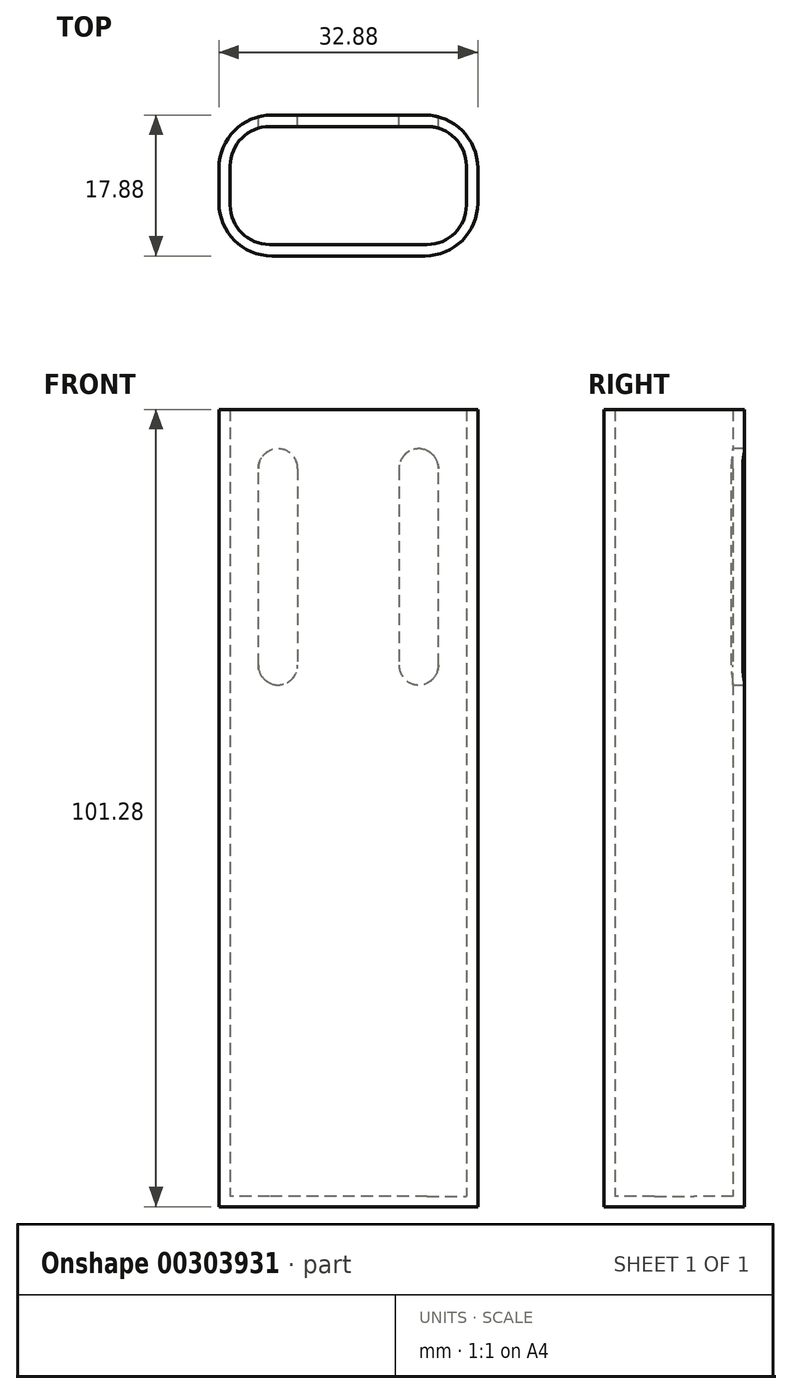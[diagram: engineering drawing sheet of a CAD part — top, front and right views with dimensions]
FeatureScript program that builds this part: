
annotation { "Feature Type Name" : "Feature", "Feature Type Description" : "" }
export const myFeature = defineFeature(function(context is Context, id is Id, definition is map)
    precondition{}
    {
        {
            var Q0;
            Q0=qCreatedBy(makeId("Top.planeOp"),FACE);
            var sketch = newSketch(context, id + "F0", { "sketchPlane" : qUnion([Q0])});
            skLineSegment(sketch, "E0.bottom", {"start": v(0, 0) * mm, "end": v(32.88, 0) * mm});
            skLineSegment(sketch, "E0.top", {"start": v(0, 17.88) * mm, "end": v(32.88, 17.88) * mm});
            skLineSegment(sketch, "E0.left", {"start": v(0, 0) * mm, "end": v(0, 17.88) * mm});
            skLineSegment(sketch, "E0.right", {"start": v(32.88, 0) * mm, "end": v(32.88, 17.88) * mm});
            skSolve(sketch);
        }
        {
            var Q0;
            Q0 = qSketchRegion(id + "F0", true);
            extrude(context, id + "F1", {"entities" : qUnion([Q0]), "depth" : (.32 * 4) * mm});
        }
        {
            var Q0;
            Q0=makeQuery(id+"F1.opExtrude","CAP_FACE",FACE,{"disambiguationData":[OSD([sQuery(id+"F0.wireOp",EDGE,"E0.bottom"),sQuery(id+"F0.wireOp",EDGE,"E0.top"),sQuery(id+"F0.wireOp",EDGE,"E0.left"),sQuery(id+"F0.wireOp",EDGE,"E0.right")])],"isStart":false});
            var sketch = newSketch(context, id + "F2", { "sketchPlane" : qUnion([Q0])});
            skLineSegment(sketch, "E1.0.0", {"start": v(32.88, 17.88) * mm, "end": v(0, 17.88) * mm});
            skLineSegment(sketch, "E1.0.1", {"start": v(0, 17.88) * mm, "end": v(0, 0) * mm});
            skLineSegment(sketch, "E1.0.2", {"start": v(0, 0) * mm, "end": v(32.88, 0) * mm});
            skLineSegment(sketch, "E1.0.3", {"start": v(32.88, 0) * mm, "end": v(32.88, 17.88) * mm});
            skLineSegment(sketch, "E2.0", {"start": v(31.44, 16.44) * mm, "end": v(1.44, 16.44) * mm});
            skLineSegment(sketch, "E2.1", {"start": v(31.44, 1.44) * mm, "end": v(31.44, 16.44) * mm});
            skLineSegment(sketch, "E2.2", {"start": v(1.44, 1.44) * mm, "end": v(31.44, 1.44) * mm});
            skLineSegment(sketch, "E2.3", {"start": v(1.44, 16.44) * mm, "end": v(1.44, 1.44) * mm});
            skSolve(sketch);
        }
        {
            var Q0;
            Q0 = qSketchRegion(id + "F2", true);
            extrude(context, id + "F3", {"entities" : qUnion([Q0]), "operationType" : NewBodyOperationType.ADD, "depth" : 100 * mm});
        }
        {
            var Q0;
            Q0=makeQuery(id+"F3.boolean.opBoolean","MERGE",FACE,{"derivedFrom":[makeQuery(id+"F1.opExtrude","SWEPT_FACE",FACE,{"disambiguationData":[OSD([sQuery(id+"F0.wireOp",EDGE,"E0.top")])]}),makeQuery(id+"F3.opExtrude","SWEPT_FACE",FACE,{"disambiguationData":[OSD([sQuery(id+"F2.wireOp",EDGE,"E1.0.0")])]})]});
            var sketch = newSketch(context, id + "F4", { "sketchPlane" : qUnion([Q0])});
            skLineSegment(sketch, "E3.bottom", {"start": v(-27.88, 96.28) * mm, "end": v(-22.88, 96.28) * mm});
            skLineSegment(sketch, "E3.top", {"start": v(-27.88, 66.28) * mm, "end": v(-22.88, 66.28) * mm});
            skLineSegment(sketch, "E3.left", {"start": v(-27.88, 96.28) * mm, "end": v(-27.88, 66.28) * mm});
            skLineSegment(sketch, "E3.right", {"start": v(-22.88, 96.28) * mm, "end": v(-22.88, 66.28) * mm});
            skLineSegment(sketch, "E4", {"start": v(-16.44, 0) * mm, "end": v(-16.44, 101.28) * mm, "construction": true});
            skLineSegment(sketch, "E5.MirrorCS", {"start": v(-10, 96.28) * mm, "end": v(-10, 66.28) * mm});
            skLineSegment(sketch, "E6.MirrorCS", {"start": v(-5, 96.28) * mm, "end": v(-5, 66.28) * mm});
            skLineSegment(sketch, "E7.MirrorCS", {"start": v(-5, 96.28) * mm, "end": v(-10, 96.28) * mm});
            skLineSegment(sketch, "E8.MirrorCS", {"start": v(-5, 66.28) * mm, "end": v(-10, 66.28) * mm});
            skSolve(sketch);
        }
        {
            var Q0;
            Q0 = qSketchRegion(id + "F4", true);
            extrude(context, id + "F5", {"entities" : qUnion([Q0]), "operationType" : NewBodyOperationType.REMOVE, "endBound" : BoundingType.UP_TO_NEXT, "oppositeDirection" : true, "depth" : 25 * mm});
        }
        {
            var Q0;
            Q0=makeQuery(id+"F3.opExtrude","SWEPT_EDGE",EDGE,{"disambiguationData":[OSD([sQuery(id+"F2.wireOp",EDGE,"E2.2"),sQuery(id+"F2.wireOp",EDGE,"E2.3")])]});
            var Q1;
            Q1=makeQuery(id+"F3.opExtrude","SWEPT_EDGE",EDGE,{"disambiguationData":[OSD([sQuery(id+"F2.wireOp",EDGE,"E2.1"),sQuery(id+"F2.wireOp",EDGE,"E2.2")])]});
            var Q2;
            Q2=makeQuery(id+"F3.opExtrude","SWEPT_EDGE",EDGE,{"disambiguationData":[OSD([sQuery(id+"F2.wireOp",EDGE,"E2.0"),sQuery(id+"F2.wireOp",EDGE,"E2.1")])]});
            var Q3;
            Q3=makeQuery(id+"F3.opExtrude","SWEPT_EDGE",EDGE,{"disambiguationData":[OSD([sQuery(id+"F2.wireOp",EDGE,"E2.0"),sQuery(id+"F2.wireOp",EDGE,"E2.3")])]});
            fillet(context, id + "F6", {"entities" : qUnion([Q0, Q1, Q2, Q3]), "radius" : 5 * mm, "tangentPropagation" : true, "allowEdgeOverflow" : false});
        }
        {
            var Q0;
            Q0=makeQuery(id+"F3.boolean.opBoolean","MERGE",EDGE,{"derivedFrom":[makeQuery(id+"F1.opExtrude","SWEPT_EDGE",EDGE,{"disambiguationData":[OSD([sQuery(id+"F0.wireOp",EDGE,"E0.bottom"),sQuery(id+"F0.wireOp",EDGE,"E0.right")])]}),makeQuery(id+"F3.opExtrude","SWEPT_EDGE",EDGE,{"disambiguationData":[OSD([sQuery(id+"F2.wireOp",EDGE,"E1.0.2"),sQuery(id+"F2.wireOp",EDGE,"E1.0.3")])]})]});
            var Q1;
            Q1=makeQuery(id+"F3.boolean.opBoolean","MERGE",EDGE,{"derivedFrom":[makeQuery(id+"F1.opExtrude","SWEPT_EDGE",EDGE,{"disambiguationData":[OSD([sQuery(id+"F0.wireOp",EDGE,"E0.top"),sQuery(id+"F0.wireOp",EDGE,"E0.right")])]}),makeQuery(id+"F3.opExtrude","SWEPT_EDGE",EDGE,{"disambiguationData":[OSD([sQuery(id+"F2.wireOp",EDGE,"E1.0.0"),sQuery(id+"F2.wireOp",EDGE,"E1.0.3")])]})]});
            var Q2;
            Q2=makeQuery(id+"F3.boolean.opBoolean","MERGE",EDGE,{"derivedFrom":[makeQuery(id+"F1.opExtrude","SWEPT_EDGE",EDGE,{"disambiguationData":[OSD([sQuery(id+"F0.wireOp",EDGE,"E0.bottom"),sQuery(id+"F0.wireOp",EDGE,"E0.left")])]}),makeQuery(id+"F3.opExtrude","SWEPT_EDGE",EDGE,{"disambiguationData":[OSD([sQuery(id+"F2.wireOp",EDGE,"E1.0.1"),sQuery(id+"F2.wireOp",EDGE,"E1.0.2")])]})]});
            var Q3;
            Q3=makeQuery(id+"F3.boolean.opBoolean","MERGE",EDGE,{"derivedFrom":[makeQuery(id+"F1.opExtrude","SWEPT_EDGE",EDGE,{"disambiguationData":[OSD([sQuery(id+"F0.wireOp",EDGE,"E0.top"),sQuery(id+"F0.wireOp",EDGE,"E0.left")])]}),makeQuery(id+"F3.opExtrude","SWEPT_EDGE",EDGE,{"disambiguationData":[OSD([sQuery(id+"F2.wireOp",EDGE,"E1.0.0"),sQuery(id+"F2.wireOp",EDGE,"E1.0.1")])]})]});
            fillet(context, id + "F7", {"entities" : qUnion([Q0, Q1, Q2, Q3]), "radius" : 6.72 * mm, "tangentPropagation" : true, "allowEdgeOverflow" : false});
        }
        {
            var Q0;
            Q0=makeQuery(id+"F5.boolean.opBoolean","COPY",EDGE,{"derivedFrom":makeQuery(id+"F5.opExtrude","SWEPT_EDGE",EDGE,{"disambiguationData":[OSD([sQuery(id+"F4.wireOp",EDGE,"E3.bottom"),sQuery(id+"F4.wireOp",EDGE,"E3.left")])]})});
            var Q1;
            Q1=makeQuery(id+"F5.boolean.opBoolean","COPY",EDGE,{"derivedFrom":makeQuery(id+"F5.opExtrude","SWEPT_EDGE",EDGE,{"disambiguationData":[OSD([sQuery(id+"F4.wireOp",EDGE,"E5.MirrorCS"),sQuery(id+"F4.wireOp",EDGE,"E7.MirrorCS")])]})});
            var Q2;
            Q2=makeQuery(id+"F5.boolean.opBoolean","COPY",EDGE,{"derivedFrom":makeQuery(id+"F5.opExtrude","SWEPT_EDGE",EDGE,{"disambiguationData":[OSD([sQuery(id+"F4.wireOp",EDGE,"E3.top"),sQuery(id+"F4.wireOp",EDGE,"E3.left")])]})});
            var Q3;
            Q3=makeQuery(id+"F5.boolean.opBoolean","COPY",EDGE,{"derivedFrom":makeQuery(id+"F5.opExtrude","SWEPT_EDGE",EDGE,{"disambiguationData":[OSD([sQuery(id+"F4.wireOp",EDGE,"E5.MirrorCS"),sQuery(id+"F4.wireOp",EDGE,"E8.MirrorCS")])]})});
            var Q4;
            Q4=makeQuery(id+"F5.boolean.opBoolean","COPY",EDGE,{"derivedFrom":makeQuery(id+"F5.opExtrude","SWEPT_EDGE",EDGE,{"disambiguationData":[OSD([sQuery(id+"F4.wireOp",EDGE,"E3.bottom"),sQuery(id+"F4.wireOp",EDGE,"E3.right")])]})});
            var Q5;
            Q5=makeQuery(id+"F5.boolean.opBoolean","COPY",EDGE,{"derivedFrom":makeQuery(id+"F5.opExtrude","SWEPT_EDGE",EDGE,{"disambiguationData":[OSD([sQuery(id+"F4.wireOp",EDGE,"E6.MirrorCS"),sQuery(id+"F4.wireOp",EDGE,"E7.MirrorCS")])]})});
            var Q6;
            Q6=makeQuery(id+"F5.boolean.opBoolean","COPY",EDGE,{"derivedFrom":makeQuery(id+"F5.opExtrude","SWEPT_EDGE",EDGE,{"disambiguationData":[OSD([sQuery(id+"F4.wireOp",EDGE,"E3.top"),sQuery(id+"F4.wireOp",EDGE,"E3.right")])]})});
            var Q7;
            Q7=makeQuery(id+"F5.boolean.opBoolean","COPY",EDGE,{"derivedFrom":makeQuery(id+"F5.opExtrude","SWEPT_EDGE",EDGE,{"disambiguationData":[OSD([sQuery(id+"F4.wireOp",EDGE,"E6.MirrorCS"),sQuery(id+"F4.wireOp",EDGE,"E8.MirrorCS")])]})});
            fillet(context, id + "F8", {"entities" : qUnion([Q0, Q1, Q2, Q3, Q4, Q5, Q6, Q7]), "radius" : 2.5 * mm, "tangentPropagation" : true, "allowEdgeOverflow" : false});
        }
    });
